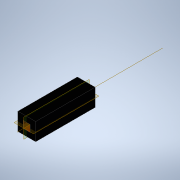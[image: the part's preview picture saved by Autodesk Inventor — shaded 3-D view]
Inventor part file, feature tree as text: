
AUTODESK INVENTOR PART (.ipt)
format: ipt  version: 2020 (Build 240168000, 168)  size: 102,912 bytes
history: native  units: in
note: dims shown in document units (in); Inventor stores cm internally (conversion verified against a paired STEP export)
features: other x2, plane x2
ambient origin geometry x8: Origin, YZ Plane, XZ Plane, XY Plane, X Axis, Y Axis, Z Axis, Center Point
bodies: Solid1 (feature_tree)
feature tree (4):
  other  "Part1"
  other  "Work Axis1"
  plane  "Work Plane1"
  plane  "Work Plane2"
